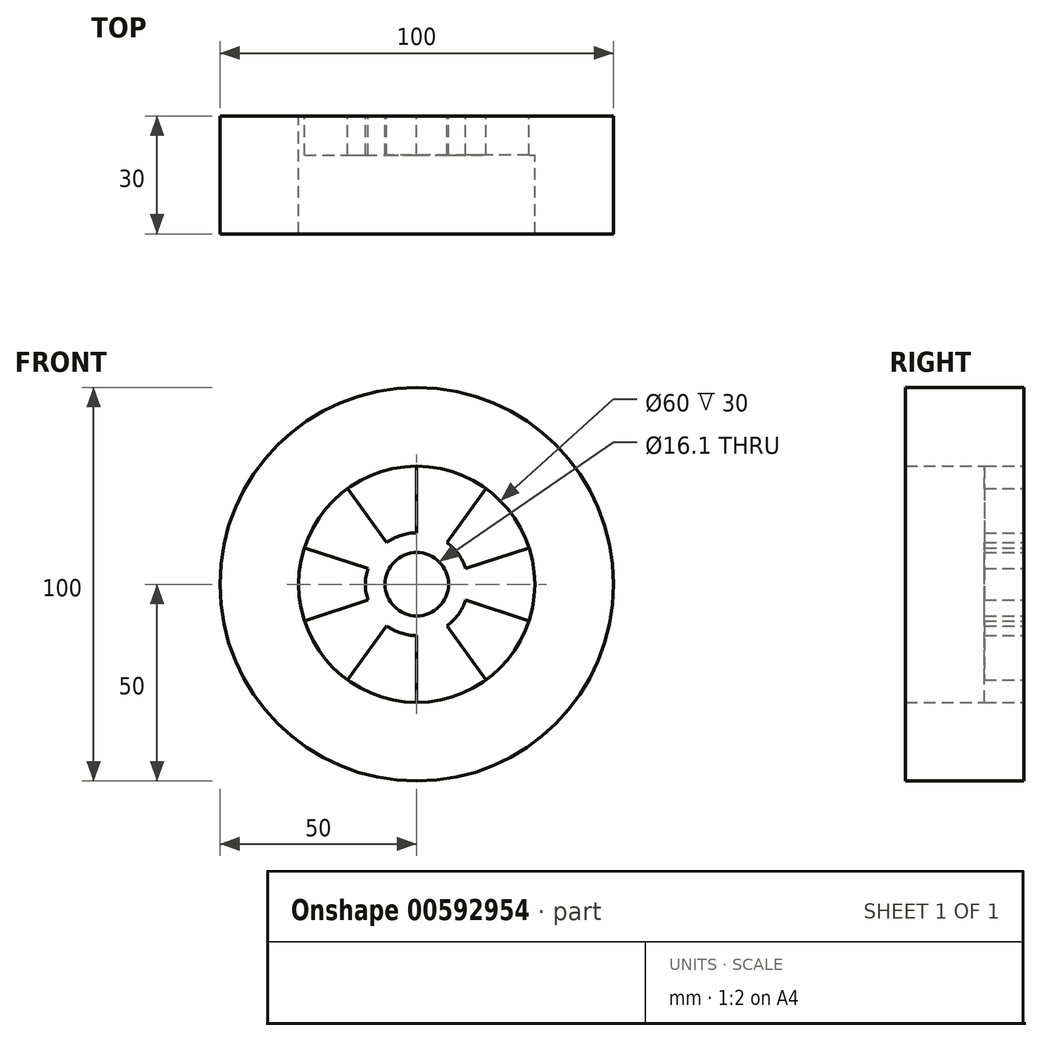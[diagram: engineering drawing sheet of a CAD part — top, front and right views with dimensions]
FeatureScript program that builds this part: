
annotation { "Feature Type Name" : "Feature", "Feature Type Description" : "" }
export const myFeature = defineFeature(function(context is Context, id is Id, definition is map)
    precondition{}
    {
        {
            var Q0;
            Q0=qCreatedBy(makeId("Front.planeOp"),FACE);
            var sketch = newSketch(context, id + "F0", { "sketchPlane" : qUnion([Q0])});
            skCircle(sketch, "E0", {"center": v(0, 0) * mm, "radius": 30 * mm});
            skCircle(sketch, "E1", {"center": v(0, 0) * mm, "radius": 8.05 * mm});
            skCircle(sketch, "E2.0", {"center": v(0, 0) * mm, "radius": 50 * mm});
            skLineSegment(sketch, "E3", {"start": v(0, 30) * mm, "end": v(0, 8.05) * mm});
            skLineSegment(sketch, "E4.1.0", {"start": v(-17.63, 24.27) * mm, "end": v(-4.73, 6.51) * mm});
            skLineSegment(sketch, "E4.2.0", {"start": v(-28.53, 9.27) * mm, "end": v(-7.66, 2.49) * mm});
            skLineSegment(sketch, "E4.3.0", {"start": v(-28.53, -9.27) * mm, "end": v(-7.66, -2.49) * mm});
            skLineSegment(sketch, "E4.4.0", {"start": v(-17.63, -24.27) * mm, "end": v(-4.73, -6.51) * mm});
            skLineSegment(sketch, "E4.5.0", {"start": v(0, -30) * mm, "end": v(0, -8.05) * mm});
            skLineSegment(sketch, "E4.6.0", {"start": v(17.63, -24.27) * mm, "end": v(4.73, -6.51) * mm});
            skLineSegment(sketch, "E4.7.0", {"start": v(28.53, -9.27) * mm, "end": v(7.66, -2.49) * mm});
            skLineSegment(sketch, "E4.8.0", {"start": v(28.53, 9.27) * mm, "end": v(7.66, 2.49) * mm});
            skLineSegment(sketch, "E4.9.0", {"start": v(17.63, 24.27) * mm, "end": v(4.73, 6.51) * mm});
            skCircle(sketch, "E5.0", {"center": v(0, 0) * mm, "radius": 13.05 * mm});
            skSolve(sketch);
        }
        {
            var Q0;
            Q0=makeQuery(id+"F0.imprint","IMPRINT",FACE,{"disambiguationData":[TD([[makeQuery(id+"F0.imprint","IMPRINT",EDGE,{"derivedFrom":sQuery(id+"F0.wireOp",EDGE,"E2.0")}),1.0]])]});
            extrude(context, id + "F1", {"entities" : qUnion([Q0]), "depth" : 30 * mm, "offsetDistance" : 25 * mm});
        }
        {
            var Q0;
            {var subQ0=sQuery(id+"F0.wireOp",EDGE,"E4.1.0");var subQ1=sQuery(id+"F0.wireOp",EDGE,"E0");var subQ2=makeQuery(id+"F0.imprint","INTERSECT",VERTEX,{"derivedFrom":[subQ1,subQ0]});Q0=makeQuery(id+"F0.imprint","IMPRINT",FACE,{"disambiguationData":[TD([[makeQuery(id+"F0.imprint","IMPRINT",EDGE,{"disambiguationData":[TD([[subQ2,-1.0]])],"derivedFrom":subQ1}),1.0]])]});}
            var Q1;
            {var subQ0=sQuery(id+"F0.wireOp",EDGE,"E4.1.0");var subQ1=sQuery(id+"F0.wireOp",EDGE,"E1");var subQ2=makeQuery(id+"F0.imprint","INTERSECT",VERTEX,{"derivedFrom":[subQ1,subQ0]});Q1=makeQuery(id+"F0.imprint","IMPRINT",FACE,{"disambiguationData":[TD([[makeQuery(id+"F0.imprint","IMPRINT",EDGE,{"disambiguationData":[TD([[subQ2,-1.0]])],"derivedFrom":subQ1}),-1.0]])]});}
            var Q2;
            {var subQ0=sQuery(id+"F0.wireOp",EDGE,"E3");var subQ1=sQuery(id+"F0.wireOp",EDGE,"E1");var subQ2=makeQuery(id+"F0.imprint","INTERSECT",VERTEX,{"derivedFrom":[subQ1,subQ0]});Q2=makeQuery(id+"F0.imprint","IMPRINT",FACE,{"disambiguationData":[TD([[makeQuery(id+"F0.imprint","IMPRINT",EDGE,{"disambiguationData":[TD([[subQ2,-1.0]])],"derivedFrom":subQ1}),-1.0]])]});}
            var Q3;
            {var subQ0=sQuery(id+"F0.wireOp",EDGE,"E3");var subQ1=sQuery(id+"F0.wireOp",EDGE,"E1");var subQ2=makeQuery(id+"F0.imprint","INTERSECT",VERTEX,{"derivedFrom":[subQ1,subQ0]});Q3=makeQuery(id+"F0.imprint","IMPRINT",FACE,{"disambiguationData":[TD([[makeQuery(id+"F0.imprint","IMPRINT",EDGE,{"disambiguationData":[TD([[subQ2,1.0]])],"derivedFrom":subQ1}),-1.0]])]});}
            var Q4;
            {var subQ0=sQuery(id+"F0.wireOp",EDGE,"E4.8.0");var subQ1=sQuery(id+"F0.wireOp",EDGE,"E1");var subQ2=makeQuery(id+"F0.imprint","INTERSECT",VERTEX,{"derivedFrom":[subQ1,subQ0]});Q4=makeQuery(id+"F0.imprint","IMPRINT",FACE,{"disambiguationData":[TD([[makeQuery(id+"F0.imprint","IMPRINT",EDGE,{"disambiguationData":[TD([[subQ2,-1.0]])],"derivedFrom":subQ1}),-1.0]])]});}
            var Q5;
            {var subQ0=sQuery(id+"F0.wireOp",EDGE,"E4.7.0");var subQ1=sQuery(id+"F0.wireOp",EDGE,"E1");var subQ2=makeQuery(id+"F0.imprint","INTERSECT",VERTEX,{"derivedFrom":[subQ1,subQ0]});Q5=makeQuery(id+"F0.imprint","IMPRINT",FACE,{"disambiguationData":[TD([[makeQuery(id+"F0.imprint","IMPRINT",EDGE,{"disambiguationData":[TD([[subQ2,-1.0]])],"derivedFrom":subQ1}),-1.0]])]});}
            var Q6;
            {var subQ0=sQuery(id+"F0.wireOp",EDGE,"E4.6.0");var subQ1=sQuery(id+"F0.wireOp",EDGE,"E1");var subQ2=makeQuery(id+"F0.imprint","INTERSECT",VERTEX,{"derivedFrom":[subQ1,subQ0]});Q6=makeQuery(id+"F0.imprint","IMPRINT",FACE,{"disambiguationData":[TD([[makeQuery(id+"F0.imprint","IMPRINT",EDGE,{"disambiguationData":[TD([[subQ2,-1.0]])],"derivedFrom":subQ1}),-1.0]])]});}
            var Q7;
            {var subQ0=sQuery(id+"F0.wireOp",EDGE,"E4.5.0");var subQ1=sQuery(id+"F0.wireOp",EDGE,"E1");var subQ2=makeQuery(id+"F0.imprint","INTERSECT",VERTEX,{"derivedFrom":[subQ1,subQ0]});Q7=makeQuery(id+"F0.imprint","IMPRINT",FACE,{"disambiguationData":[TD([[makeQuery(id+"F0.imprint","IMPRINT",EDGE,{"disambiguationData":[TD([[subQ2,-1.0]])],"derivedFrom":subQ1}),-1.0]])]});}
            var Q8;
            {var subQ0=sQuery(id+"F0.wireOp",EDGE,"E4.4.0");var subQ1=sQuery(id+"F0.wireOp",EDGE,"E1");var subQ2=makeQuery(id+"F0.imprint","INTERSECT",VERTEX,{"derivedFrom":[subQ1,subQ0]});Q8=makeQuery(id+"F0.imprint","IMPRINT",FACE,{"disambiguationData":[TD([[makeQuery(id+"F0.imprint","IMPRINT",EDGE,{"disambiguationData":[TD([[subQ2,-1.0]])],"derivedFrom":subQ1}),-1.0]])]});}
            var Q9;
            {var subQ0=sQuery(id+"F0.wireOp",EDGE,"E4.3.0");var subQ1=sQuery(id+"F0.wireOp",EDGE,"E1");var subQ2=makeQuery(id+"F0.imprint","INTERSECT",VERTEX,{"derivedFrom":[subQ1,subQ0]});Q9=makeQuery(id+"F0.imprint","IMPRINT",FACE,{"disambiguationData":[TD([[makeQuery(id+"F0.imprint","IMPRINT",EDGE,{"disambiguationData":[TD([[subQ2,-1.0]])],"derivedFrom":subQ1}),-1.0]])]});}
            var Q10;
            {var subQ0=sQuery(id+"F0.wireOp",EDGE,"E4.2.0");var subQ1=sQuery(id+"F0.wireOp",EDGE,"E1");var subQ2=makeQuery(id+"F0.imprint","INTERSECT",VERTEX,{"derivedFrom":[subQ1,subQ0]});Q10=makeQuery(id+"F0.imprint","IMPRINT",FACE,{"disambiguationData":[TD([[makeQuery(id+"F0.imprint","IMPRINT",EDGE,{"disambiguationData":[TD([[subQ2,-1.0]])],"derivedFrom":subQ1}),-1.0]])]});}
            var Q11;
            {var subQ0=sQuery(id+"F0.wireOp",EDGE,"E4.3.0");var subQ1=sQuery(id+"F0.wireOp",EDGE,"E0");var subQ2=makeQuery(id+"F0.imprint","INTERSECT",VERTEX,{"derivedFrom":[subQ1,subQ0]});Q11=makeQuery(id+"F0.imprint","IMPRINT",FACE,{"disambiguationData":[TD([[makeQuery(id+"F0.imprint","IMPRINT",EDGE,{"disambiguationData":[TD([[subQ2,-1.0]])],"derivedFrom":subQ1}),1.0]])]});}
            var Q12;
            {var subQ0=sQuery(id+"F0.wireOp",EDGE,"E4.5.0");var subQ1=sQuery(id+"F0.wireOp",EDGE,"E0");var subQ2=makeQuery(id+"F0.imprint","INTERSECT",VERTEX,{"derivedFrom":[subQ1,subQ0]});Q12=makeQuery(id+"F0.imprint","IMPRINT",FACE,{"disambiguationData":[TD([[makeQuery(id+"F0.imprint","IMPRINT",EDGE,{"disambiguationData":[TD([[subQ2,-1.0]])],"derivedFrom":subQ1}),1.0]])]});}
            var Q13;
            {var subQ0=sQuery(id+"F0.wireOp",EDGE,"E4.7.0");var subQ1=sQuery(id+"F0.wireOp",EDGE,"E0");var subQ2=makeQuery(id+"F0.imprint","INTERSECT",VERTEX,{"derivedFrom":[subQ1,subQ0]});Q13=makeQuery(id+"F0.imprint","IMPRINT",FACE,{"disambiguationData":[TD([[makeQuery(id+"F0.imprint","IMPRINT",EDGE,{"disambiguationData":[TD([[subQ2,-1.0]])],"derivedFrom":subQ1}),1.0]])]});}
            var Q14;
            {var subQ0=sQuery(id+"F0.wireOp",EDGE,"E3");var subQ1=sQuery(id+"F0.wireOp",EDGE,"E0");var subQ2=makeQuery(id+"F0.imprint","INTERSECT",VERTEX,{"derivedFrom":[subQ1,subQ0]});Q14=makeQuery(id+"F0.imprint","IMPRINT",FACE,{"disambiguationData":[TD([[makeQuery(id+"F0.imprint","IMPRINT",EDGE,{"disambiguationData":[TD([[subQ2,1.0]])],"derivedFrom":subQ1}),1.0]])]});}
            extrude(context, id + "F2", {"entities" : qUnion([Q0, Q1, Q2, Q3, Q4, Q5, Q6, Q7, Q8, Q9, Q10, Q11, Q12, Q13, Q14]), "operationType" : NewBodyOperationType.ADD, "depth" : 10 * mm, "offsetDistance" : 25 * mm});
        }
    });
